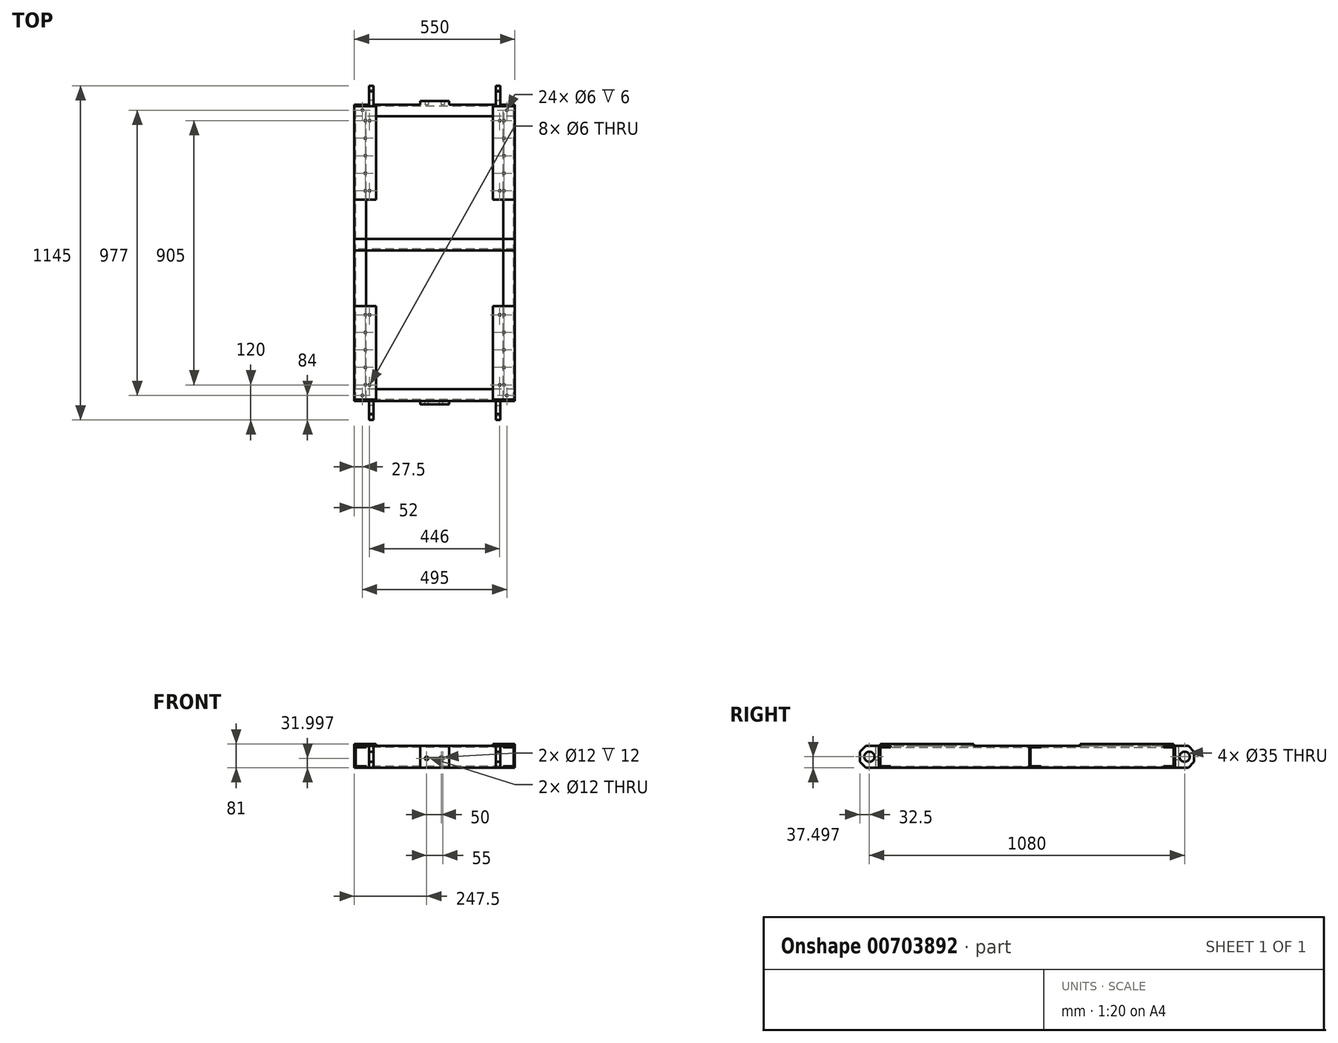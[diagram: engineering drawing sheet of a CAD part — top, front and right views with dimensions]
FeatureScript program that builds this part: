
annotation { "Feature Type Name" : "Feature", "Feature Type Description" : "" }
export const myFeature = defineFeature(function(context is Context, id is Id, definition is map)
    precondition{}
    {
        {
            var Q0;
            Q0=qCreatedBy(makeId("Front.planeOp"),FACE);
            var sketch = newSketch(context, id + "F0", { "sketchPlane" : qUnion([Q0])});
            skLineSegment(sketch, "E0", {"start": v(0, 32.91) * mm, "end": v(0, -42.47) * mm});
            skLineSegment(sketch, "E1", {"start": v(0, -42.47) * mm, "end": v(40, -42.47) * mm});
            skLineSegment(sketch, "E2", {"start": v(40, -42.47) * mm, "end": v(40, -37.47) * mm});
            skLineSegment(sketch, "E3", {"start": v(40, -37.47) * mm, "end": v(5, -37.47) * mm});
            skLineSegment(sketch, "E4", {"start": v(5, -37.47) * mm, "end": v(5, 27.53) * mm});
            skLineSegment(sketch, "E5", {"start": v(5, 27.53) * mm, "end": v(40, 27.53) * mm});
            skLineSegment(sketch, "E6", {"start": v(40, 27.53) * mm, "end": v(40, 32.53) * mm});
            skLineSegment(sketch, "E7", {"start": v(40, 32.53) * mm, "end": v(0, 32.53) * mm});
            skLineSegment(sketch, "E8.MirrorCS", {"start": v(510, -37.47) * mm, "end": v(545, -37.47) * mm});
            skLineSegment(sketch, "E9.MirrorCS", {"start": v(545, -37.47) * mm, "end": v(545, 27.53) * mm});
            skLineSegment(sketch, "E10.MirrorCS", {"start": v(545, 27.53) * mm, "end": v(510, 27.53) * mm});
            skLineSegment(sketch, "E11.MirrorCS", {"start": v(510, 27.53) * mm, "end": v(510, 32.53) * mm});
            skLineSegment(sketch, "E12.MirrorCS", {"start": v(510, 32.53) * mm, "end": v(550, 32.53) * mm});
            skLineSegment(sketch, "E13.MirrorCS", {"start": v(510, -42.47) * mm, "end": v(510, -37.47) * mm});
            skLineSegment(sketch, "E14.MirrorCS", {"start": v(550, 32.91) * mm, "end": v(550, -42.47) * mm});
            skLineSegment(sketch, "E15.MirrorCS", {"start": v(550, -42.47) * mm, "end": v(510, -42.47) * mm});
            skSolve(sketch);
        }
        {
            var Q0;
            {var subQ0=sQuery(id+"F0.wireOp",EDGE,"E1");Q0=makeQuery(id+"F0.imprint","IMPRINT",FACE,{"disambiguationData":[TD([[makeQuery(id+"F0.imprint","IMPRINT",EDGE,{"derivedFrom":subQ0}),1.0]])]});}
            var Q1;
            Q1=makeQuery(id+"F0.imprint","IMPRINT",FACE,{"disambiguationData":[TD([[makeQuery(id+"F0.imprint","IMPRINT",EDGE,{"derivedFrom":sQuery(id+"F0.wireOp",EDGE,"E8.MirrorCS")}),-1.0]])]});
            extrude(context, id + "F1", {"entities" : qUnion([Q0, Q1]), "depth" : 1015 * mm, "offsetDistance" : 25 * mm});
        }
        {
            var Q0;
            Q0=qCreatedBy(makeId("Right.planeOp"),FACE);
            var sketch = newSketch(context, id + "F2", { "sketchPlane" : qUnion([Q0])});
            skLineSegment(sketch, "E16", {"start": v(0, -42.47) * mm, "end": v(0, 32.53) * mm});
            skLineSegment(sketch, "E17", {"start": v(-40, 32.53) * mm, "end": v(-40, 27.53) * mm});
            skLineSegment(sketch, "E18", {"start": v(-40, 27.53) * mm, "end": v(-5, 27.53) * mm});
            skLineSegment(sketch, "E19", {"start": v(-5, 27.53) * mm, "end": v(-5, -37.47) * mm});
            skLineSegment(sketch, "E20", {"start": v(-5, -37.47) * mm, "end": v(-40, -37.47) * mm});
            skLineSegment(sketch, "E21", {"start": v(-40, -37.47) * mm, "end": v(-40, -42.47) * mm});
            skLineSegment(sketch, "E22", {"start": v(-40, -42.47) * mm, "end": v(0, -42.47) * mm});
            skLineSegment(sketch, "E23", {"start": v(-40, 32.53) * mm, "end": v(0, 32.53) * mm});
            skLineSegment(sketch, "E24.MirrorCS", {"start": v(-975, 32.53) * mm, "end": v(-975, 27.53) * mm});
            skLineSegment(sketch, "E25.MirrorCS", {"start": v(-975, -37.47) * mm, "end": v(-975, -42.47) * mm});
            skLineSegment(sketch, "E26.MirrorCS", {"start": v(-975, 27.53) * mm, "end": v(-1010, 27.53) * mm});
            skLineSegment(sketch, "E27.MirrorCS", {"start": v(-1010, 27.53) * mm, "end": v(-1010, -37.47) * mm});
            skLineSegment(sketch, "E28.MirrorCS", {"start": v(-1010, -37.47) * mm, "end": v(-975, -37.47) * mm});
            skLineSegment(sketch, "E29.MirrorCS", {"start": v(-975, 32.53) * mm, "end": v(-1015, 32.53) * mm});
            skLineSegment(sketch, "E30.MirrorCS", {"start": v(-1015, -42.47) * mm, "end": v(-1015, 32.53) * mm});
            skLineSegment(sketch, "E31.MirrorCS", {"start": v(-975, -42.47) * mm, "end": v(-1015, -42.47) * mm});
            skLineSegment(sketch, "E32.MirrorCS", {"start": v(-460, 32.53) * mm, "end": v(-460, 27.53) * mm});
            skLineSegment(sketch, "E33.MirrorCS", {"start": v(-460, -37.47) * mm, "end": v(-460, -42.47) * mm});
            skLineSegment(sketch, "E34.MirrorCS", {"start": v(-460, 27.53) * mm, "end": v(-495, 27.53) * mm});
            skLineSegment(sketch, "E35.MirrorCS", {"start": v(-495, 27.53) * mm, "end": v(-495, -37.47) * mm});
            skLineSegment(sketch, "E36.MirrorCS", {"start": v(-495, -37.47) * mm, "end": v(-460, -37.47) * mm});
            skLineSegment(sketch, "E37.MirrorCS", {"start": v(-460, 32.53) * mm, "end": v(-500, 32.53) * mm});
            skLineSegment(sketch, "E38.MirrorCS", {"start": v(-500, -42.47) * mm, "end": v(-500, 32.53) * mm});
            skLineSegment(sketch, "E39.MirrorCS", {"start": v(-460, -42.47) * mm, "end": v(-500, -42.47) * mm});
            skPoint(sketch, "E40", {"position": v(-1015, -42.47) * mm});
            skSolve(sketch);
        }
        {
            var Q0;
            Q0 = qSketchRegion(id + "F2", true);
            extrude(context, id + "F3", {"entities" : qUnion([Q0]), "depth" : 550 * mm, "offsetDistance" : 25 * mm});
        }
        {
            var Q0;
            Q0=makeQuery(id+"F1.opExtrude","SWEPT_FACE",FACE,{"disambiguationData":[OSD([sQuery(id+"F0.wireOp",EDGE,"E7")])]});
            var sketch = newSketch(context, id + "F4", { "sketchPlane" : qUnion([Q0])});
            skLineSegment(sketch, "E41.bottom", {"start": v(0, -5) * mm, "end": v(75, -5) * mm});
            skLineSegment(sketch, "E41.top", {"start": v(0, -325) * mm, "end": v(75, -325) * mm});
            skLineSegment(sketch, "E41.left", {"start": v(0, -5) * mm, "end": v(0, -325) * mm});
            skLineSegment(sketch, "E41.right", {"start": v(75, -5) * mm, "end": v(75, -325) * mm});
            skLineSegment(sketch, "E42.MirrorCS", {"start": v(550, -5) * mm, "end": v(475, -5) * mm});
            skLineSegment(sketch, "E43.MirrorCS", {"start": v(550, -325) * mm, "end": v(475, -325) * mm});
            skLineSegment(sketch, "E44.MirrorCS", {"start": v(550, -5) * mm, "end": v(550, -325) * mm});
            skLineSegment(sketch, "E45.MirrorCS", {"start": v(475, -5) * mm, "end": v(475, -325) * mm});
            skLineSegment(sketch, "E46.MirrorCS", {"start": v(0, -1010) * mm, "end": v(75, -1010) * mm});
            skLineSegment(sketch, "E47.MirrorCS", {"start": v(0, -690) * mm, "end": v(75, -690) * mm});
            skLineSegment(sketch, "E48.MirrorCS", {"start": v(0, -1010) * mm, "end": v(0, -690) * mm});
            skLineSegment(sketch, "E49.MirrorCS", {"start": v(75, -1010) * mm, "end": v(75, -690) * mm});
            skLineSegment(sketch, "E50.MirrorCS", {"start": v(475, -1010) * mm, "end": v(475, -690) * mm});
            skLineSegment(sketch, "E51.MirrorCS", {"start": v(550, -1010) * mm, "end": v(550, -690) * mm});
            skLineSegment(sketch, "E52.MirrorCS", {"start": v(550, -690) * mm, "end": v(475, -690) * mm});
            skLineSegment(sketch, "E53.MirrorCS", {"start": v(550, -1010) * mm, "end": v(475, -1010) * mm});
            skCircle(sketch, "E54", {"center": v(37.5, -55) * mm, "radius": 3 * mm});
            skCircle(sketch, "E55", {"center": v(52, -55) * mm, "radius": 3 * mm});
            skCircle(sketch, "E56", {"center": v(37.5, -115) * mm, "radius": 3 * mm});
            skCircle(sketch, "E57", {"center": v(37.5, -175) * mm, "radius": 3 * mm});
            skCircle(sketch, "E58", {"center": v(37.5, -235) * mm, "radius": 3 * mm});
            skCircle(sketch, "E59", {"center": v(37.5, -295) * mm, "radius": 3 * mm});
            skCircle(sketch, "E60", {"center": v(52, -295) * mm, "radius": 3 * mm});
            skCircle(sketch, "E61", {"center": v(27.5, -19) * mm, "radius": 3 * mm});
            skLineSegment(sketch, "E62", {"start": v(275, 0) * mm, "end": v(275, -1135.71) * mm});
            skCircle(sketch, "E63.MirrorC", {"center": v(512.5, -115) * mm, "radius": 3 * mm});
            skCircle(sketch, "E64.MirrorC", {"center": v(512.5, -295) * mm, "radius": 3 * mm});
            skCircle(sketch, "E65.MirrorC", {"center": v(498, -55) * mm, "radius": 3 * mm});
            skCircle(sketch, "E66.MirrorC", {"center": v(512.5, -175) * mm, "radius": 3 * mm});
            skCircle(sketch, "E67.MirrorC", {"center": v(522.5, -19) * mm, "radius": 3 * mm});
            skCircle(sketch, "E68.MirrorC", {"center": v(512.5, -55) * mm, "radius": 3 * mm});
            skCircle(sketch, "E69.MirrorC", {"center": v(498, -295) * mm, "radius": 3 * mm});
            skCircle(sketch, "E70.MirrorC", {"center": v(512.5, -235) * mm, "radius": 3 * mm});
            skLineSegment(sketch, "E71", {"start": v(0, -507.5) * mm, "end": v(621.6, -507.5) * mm});
            skCircle(sketch, "E72.MirrorC", {"center": v(37.5, -840) * mm, "radius": 3 * mm});
            skCircle(sketch, "E73.MirrorC", {"center": v(52, -720) * mm, "radius": 3 * mm});
            skCircle(sketch, "E74.MirrorC", {"center": v(27.5, -996) * mm, "radius": 3 * mm});
            skCircle(sketch, "E75.MirrorC", {"center": v(37.5, -720) * mm, "radius": 3 * mm});
            skCircle(sketch, "E76.MirrorC", {"center": v(52, -960) * mm, "radius": 3 * mm});
            skCircle(sketch, "E77.MirrorC", {"center": v(37.5, -900) * mm, "radius": 3 * mm});
            skCircle(sketch, "E78.MirrorC", {"center": v(37.5, -780) * mm, "radius": 3 * mm});
            skCircle(sketch, "E79.MirrorC", {"center": v(37.5, -960) * mm, "radius": 3 * mm});
            skCircle(sketch, "E80.MirrorC", {"center": v(512.5, -960) * mm, "radius": 3 * mm});
            skCircle(sketch, "E81.MirrorC", {"center": v(512.5, -780) * mm, "radius": 3 * mm});
            skCircle(sketch, "E82.MirrorC", {"center": v(498, -960) * mm, "radius": 3 * mm});
            skCircle(sketch, "E83.MirrorC", {"center": v(512.5, -840) * mm, "radius": 3 * mm});
            skCircle(sketch, "E84.MirrorC", {"center": v(512.5, -720) * mm, "radius": 3 * mm});
            skCircle(sketch, "E85.MirrorC", {"center": v(522.5, -996) * mm, "radius": 3 * mm});
            skCircle(sketch, "E86.MirrorC", {"center": v(512.5, -900) * mm, "radius": 3 * mm});
            skCircle(sketch, "E87.MirrorC", {"center": v(498, -720) * mm, "radius": 3 * mm});
            skSolve(sketch);
        }
        {
            var Q0;
            Q0 = qSketchRegion(id + "F4", true);
            extrude(context, id + "F5", {"entities" : qUnion([Q0]), "operationType" : NewBodyOperationType.ADD, "depth" : 6 * mm, "offsetDistance" : 25 * mm});
        }
        {
            var Q0;
            Q0=qCreatedBy(makeId("Right.planeOp"),FACE);
            cPlane(context, id + "F6", {"entities" : qUnion([Q0]), "cplaneType" : CPlaneType.OFFSET, "offset" : 50 * mm, "width" : 150 * mm, "height" : 150 * mm});
        }
        {
            var Q0;
            Q0=qCreatedBy(id+"F6.planeOp",FACE);
            var sketch = newSketch(context, id + "F7", { "sketchPlane" : qUnion([Q0])});
            skLineSegment(sketch, "E88", {"start": v(0, -42.47) * mm, "end": v(45, -42.47) * mm});
            skLineSegment(sketch, "E89", {"start": v(45, -42.47) * mm, "end": v(65, -22.47) * mm});
            skLineSegment(sketch, "E90", {"start": v(65, -22.47) * mm, "end": v(65, 12.53) * mm});
            skLineSegment(sketch, "E91", {"start": v(65, 12.53) * mm, "end": v(45, 32.53) * mm});
            skLineSegment(sketch, "E92", {"start": v(45, 32.53) * mm, "end": v(0, 32.53) * mm});
            skLineSegment(sketch, "E93", {"start": v(0, 32.53) * mm, "end": v(0, -42.47) * mm});
            skCircle(sketch, "E94", {"center": v(32.5, -4.97) * mm, "radius": 17.5 * mm});
            skLineSegment(sketch, "E95.MirrorCS", {"start": v(-1080, 12.53) * mm, "end": v(-1060, 32.53) * mm});
            skLineSegment(sketch, "E96.MirrorCS", {"start": v(-1080, -22.47) * mm, "end": v(-1080, 12.53) * mm});
            skLineSegment(sketch, "E97.MirrorCS", {"start": v(-1060, -42.47) * mm, "end": v(-1080, -22.47) * mm});
            skLineSegment(sketch, "E98.MirrorCS", {"start": v(-1015, -42.47) * mm, "end": v(-1060, -42.47) * mm});
            skCircle(sketch, "E99.MirrorC", {"center": v(-1047.5, -4.97) * mm, "radius": 17.5 * mm});
            skLineSegment(sketch, "E100.MirrorCS", {"start": v(-1015, 32.53) * mm, "end": v(-1015, -42.47) * mm});
            skLineSegment(sketch, "E101.MirrorCS", {"start": v(-1060, 32.53) * mm, "end": v(-1015, 32.53) * mm});
            skSolve(sketch);
        }
        {
            var Q0;
            Q0 = qSketchRegion(id + "F7", true);
            extrude(context, id + "F8", {"entities" : qUnion([Q0]), "operationType" : NewBodyOperationType.ADD, "depth" : 16 * mm, "offsetDistance" : 25 * mm});
        }
        {
            var Q0;
            Q0=qCreatedBy(makeId("Right.planeOp"),FACE);
            cPlane(context, id + "F9", {"entities" : qUnion([Q0]), "cplaneType" : CPlaneType.OFFSET, "offset" : 500 * mm, "width" : 150 * mm, "height" : 150 * mm});
        }
        {
            var Q0;
            Q0=qCreatedBy(id+"F9.planeOp",FACE);
            var sketch = newSketch(context, id + "F10", { "sketchPlane" : qUnion([Q0])});
            skLineSegment(sketch, "E102", {"start": v(0, -42.47) * mm, "end": v(45, -42.47) * mm});
            skLineSegment(sketch, "E103", {"start": v(45, -42.47) * mm, "end": v(65, -22.47) * mm});
            skLineSegment(sketch, "E104", {"start": v(65, -22.47) * mm, "end": v(65, 12.53) * mm});
            skLineSegment(sketch, "E105", {"start": v(65, 12.53) * mm, "end": v(45, 32.53) * mm});
            skLineSegment(sketch, "E106", {"start": v(45, 32.53) * mm, "end": v(0, 32.53) * mm});
            skLineSegment(sketch, "E107", {"start": v(0, 32.53) * mm, "end": v(0, -42.47) * mm});
            skCircle(sketch, "E108", {"center": v(32.5, -4.97) * mm, "radius": 17.5 * mm});
            skCircle(sketch, "E109.MirrorC", {"center": v(-1047.5, -4.97) * mm, "radius": 17.5 * mm});
            skLineSegment(sketch, "E110.MirrorCS", {"start": v(-1060, 32.53) * mm, "end": v(-1015, 32.53) * mm});
            skLineSegment(sketch, "E111.MirrorCS", {"start": v(-1015, -42.47) * mm, "end": v(-1060, -42.47) * mm});
            skLineSegment(sketch, "E112.MirrorCS", {"start": v(-1080, -22.47) * mm, "end": v(-1080, 12.53) * mm});
            skLineSegment(sketch, "E113.MirrorCS", {"start": v(-1060, -42.47) * mm, "end": v(-1080, -22.47) * mm});
            skLineSegment(sketch, "E114.MirrorCS", {"start": v(-1080, 12.53) * mm, "end": v(-1060, 32.53) * mm});
            skLineSegment(sketch, "E115.MirrorCS", {"start": v(-1015, 32.53) * mm, "end": v(-1015, -42.47) * mm});
            skSolve(sketch);
        }
        {
            var Q0;
            Q0 = qSketchRegion(id + "F10", true);
            extrude(context, id + "F11", {"entities" : qUnion([Q0]), "operationType" : NewBodyOperationType.ADD, "oppositeDirection" : true, "depth" : 16 * mm, "offsetDistance" : 25 * mm});
        }
        {
            var Q0;
            Q0=qCreatedBy(makeId("Front.planeOp"),FACE);
            var sketch = newSketch(context, id + "F12", { "sketchPlane" : qUnion([Q0])});
            skLineSegment(sketch, "E116.bottom", {"start": v(325, -42.47) * mm, "end": v(225, -42.47) * mm});
            skLineSegment(sketch, "E116.top", {"start": v(325, 32.53) * mm, "end": v(225, 32.53) * mm});
            skLineSegment(sketch, "E116.left", {"start": v(325, -42.47) * mm, "end": v(325, 32.53) * mm});
            skLineSegment(sketch, "E116.right", {"start": v(225, -42.47) * mm, "end": v(225, 32.53) * mm});
            skCircle(sketch, "E117", {"center": v(302.5, -10.47) * mm, "radius": 6 * mm});
            skCircle(sketch, "E118", {"center": v(247.5, -10.47) * mm, "radius": 6 * mm});
            skSolve(sketch);
        }
        {
            var Q0;
            Q0 = qSketchRegion(id + "F12", true);
            extrude(context, id + "F13", {"entities" : qUnion([Q0]), "operationType" : NewBodyOperationType.ADD, "oppositeDirection" : true, "depth" : 12 * mm, "offsetDistance" : 25 * mm});
        }
        {
            var Q0;
            Q0=qCreatedBy(makeId("Front.planeOp"),FACE);
            cPlane(context, id + "F14", {"entities" : qUnion([Q0]), "cplaneType" : CPlaneType.OFFSET, "offset" : 1015 * mm, "width" : 150 * mm, "height" : 150 * mm});
        }
        {
            var Q0;
            Q0=qCreatedBy(id+"F14.planeOp",FACE);
            var sketch = newSketch(context, id + "F15", { "sketchPlane" : qUnion([Q0])});
            skLineSegment(sketch, "E119.bottom", {"start": v(225, 32.53) * mm, "end": v(325, 32.53) * mm});
            skLineSegment(sketch, "E119.top", {"start": v(225, -42.47) * mm, "end": v(325, -42.47) * mm});
            skLineSegment(sketch, "E119.left", {"start": v(225, 32.53) * mm, "end": v(225, -42.47) * mm});
            skLineSegment(sketch, "E119.right", {"start": v(325, 32.53) * mm, "end": v(325, -42.47) * mm});
            skCircle(sketch, "E120", {"center": v(247.5, -10.47) * mm, "radius": 6 * mm});
            skCircle(sketch, "E121", {"center": v(297.5, -10.47) * mm, "radius": 6 * mm});
            skSolve(sketch);
        }
        {
            var Q0;
            Q0=makeQuery(id+"F15.imprint","IMPRINT",FACE,{"disambiguationData":[TD([[makeQuery(id+"F15.imprint","IMPRINT",EDGE,{"derivedFrom":sQuery(id+"F15.wireOp",EDGE,"E119.bottom")}),-1.0]])]});
            extrude(context, id + "F16", {"entities" : qUnion([Q0]), "depth" : 12 * mm, "offsetDistance" : 25 * mm});
        }
    });
